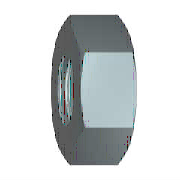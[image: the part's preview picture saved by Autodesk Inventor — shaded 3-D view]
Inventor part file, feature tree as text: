
AUTODESK INVENTOR PART (.ipt)
format: ipt  version: 2024.3 (Build 283343000, 343)  size: 162,304 bytes
history: native  units: mm (DEFAULTED — no unit token found)
features: chamfer x1, hole x1, other x1, plane x1
ambient origin geometry x7: Origin, YZ Plane, XZ Plane, X Axis, Y Axis, Z Axis, Center Point
bodies: Solid1 (feature_tree), Body (feature_tree)
feature tree (4):
  chamfer  "Chamfer1"  Distance=8.082904mm
  hole  "Thread"  [1 undecoded]
  other  "Work Axis1"
  plane  "Work Plane1"
note: 1 required parameter value undecoded (feature->parameter linkage not recoverable at this tier; creation-order binding heuristic only, values carry confidence <= 0.55)
